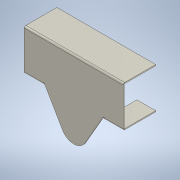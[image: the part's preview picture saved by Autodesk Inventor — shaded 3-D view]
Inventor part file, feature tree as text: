
AUTODESK INVENTOR PART (.ipt)
format: ipt  version: 2022 (Build 260153000, 153)  size: 199,680 bytes
history: native  units: mm
features: sheet_metal_op x9, sketch x4, other x4, plane x1, mirror x1
ambient origin geometry x8: Origin, YZ Plane, XZ Plane, XY Plane, X Axis, Y Axis, Z Axis, Center Point
bodies: Solid1 (feature_tree)
feature tree (19):
  sheet_metal_op  "Face1"
  sheet_metal_op  "Flange1"
  sheet_metal_op  "Flange2"
  plane  "Work Plane1"
  mirror  "Mirror1"
  sheet_metal_op  "Face2"
  sketch  "Sketch1"  dims[d0=152.4mm]
  other  "Plate1"
  sketch  "Sketch2"  dims[d1=60.0mm]
  other  "Plate2"
  sheet_metal_op  "Bend1"
  sheet_metal_op  "Corner1"
  sketch  "Sketch3"  dims[d2=1.6256mm]
  other  "Plate3"
  sheet_metal_op  "Bend2"
  sheet_metal_op  "Corner2"
  sketch  "Sketch4"  dims[d3=1.6256mm d4=0.8128mm d5=3.2512mm d6=0.79375mm d7=48.6256mm d8=90.0deg d9=0.79375mm d10=4.8768mm d11=0.8128mm d12=0.79375mm d13=1.6256mm d14=0.8128mm d15=3.2512mm d16=0.79375mm d17=29.0mm d18=0.0mm d19=48.6256mm d20=90.0deg d21=0.79375mm d22=4.8768mm d23=0.8128mm d24=0.79375mm d25=100.0mm d27=37.5mm d28=20.0mm d29=0.79375mm d30=1.6256mm d31=0.8128mm d32=3.2512mm d33=0.79375mm d202=60.0deg]
  other  "Plate4"
  sheet_metal_op  "Bend3"
